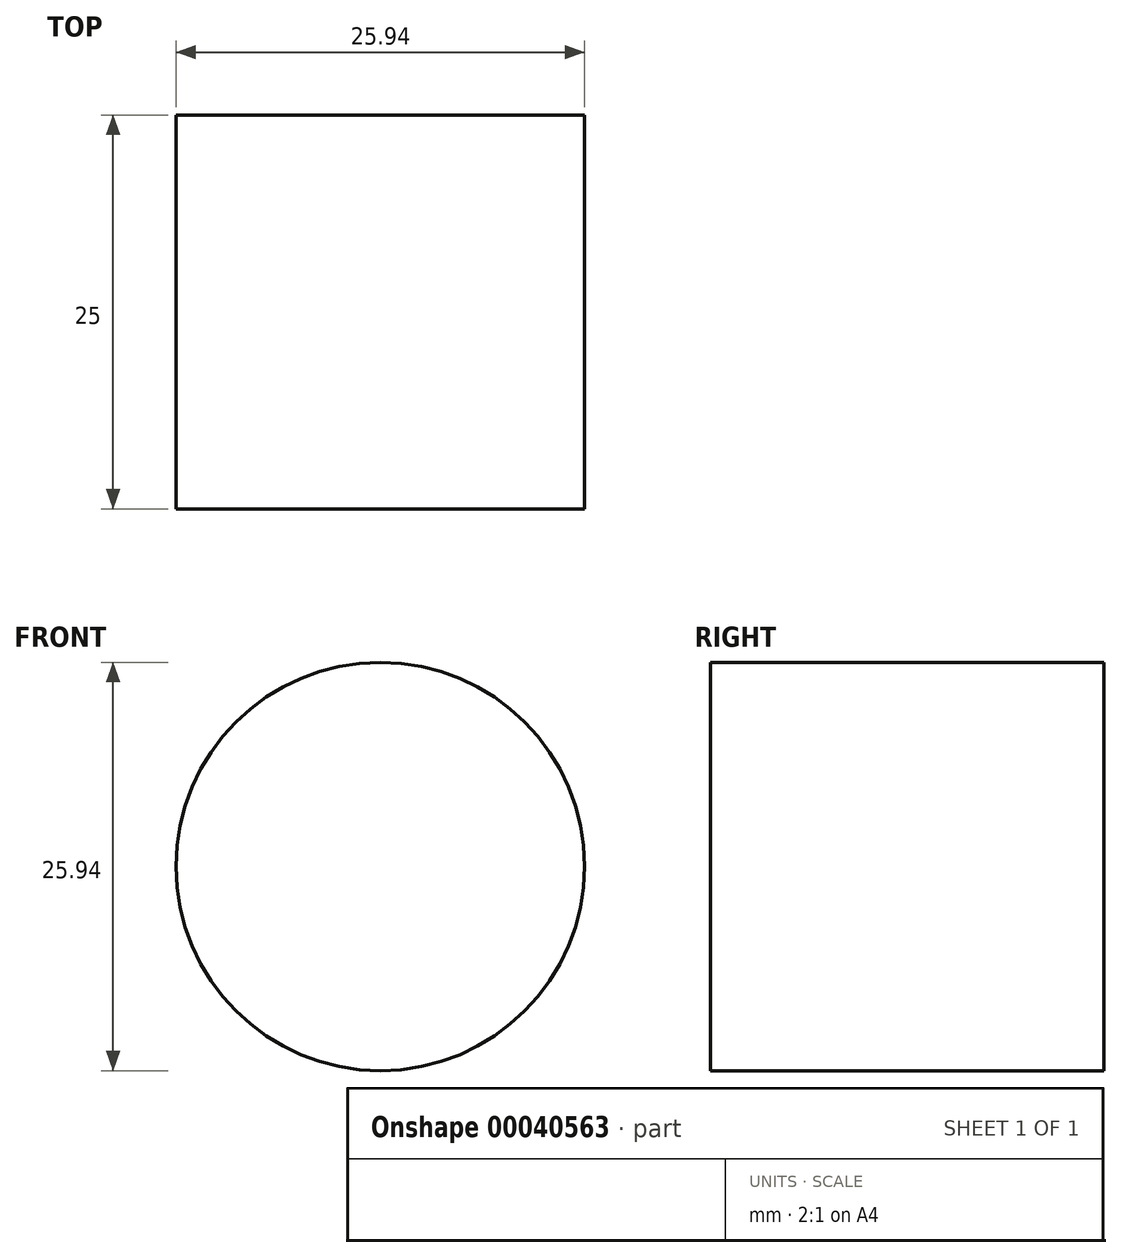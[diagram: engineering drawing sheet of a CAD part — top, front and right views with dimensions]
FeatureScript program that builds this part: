
annotation { "Feature Type Name" : "Feature", "Feature Type Description" : "" }
export const myFeature = defineFeature(function(context is Context, id is Id, definition is map)
    precondition{}
    {
        {
            var Q0;
            Q0=qCreatedBy(makeId("Front.planeOp"),FACE);
            var sketch = newSketch(context, id + "F0", { "sketchPlane" : qUnion([Q0])});
            skCircle(sketch, "E0", {"center": v(0, 0) * mm, "radius": 12.97 * mm});
            skSolve(sketch);
        }
        {
            var Q0;
            Q0=makeQuery(id+"F0.imprint","IMPRINT",FACE,{"disambiguationData":[TD([[makeQuery(id+"F0.imprint","IMPRINT",EDGE,{"derivedFrom":sQuery(id+"F0.wireOp",EDGE,"E0")}),1.0]])]});
            extrude(context, id + "F1", {"entities" : qUnion([Q0]), "depth" : 25 * mm});
        }
        {
            var Q0;
            Q0=qCreatedBy(makeId("Top.planeOp"),FACE);
            cPlane(context, id + "F2", {"entities" : qUnion([Q0]), "cplaneType" : CPlaneType.OFFSET, "offset" : 150 * mm, "width" : 150 * mm, "height" : 150 * mm});
        }
    });
